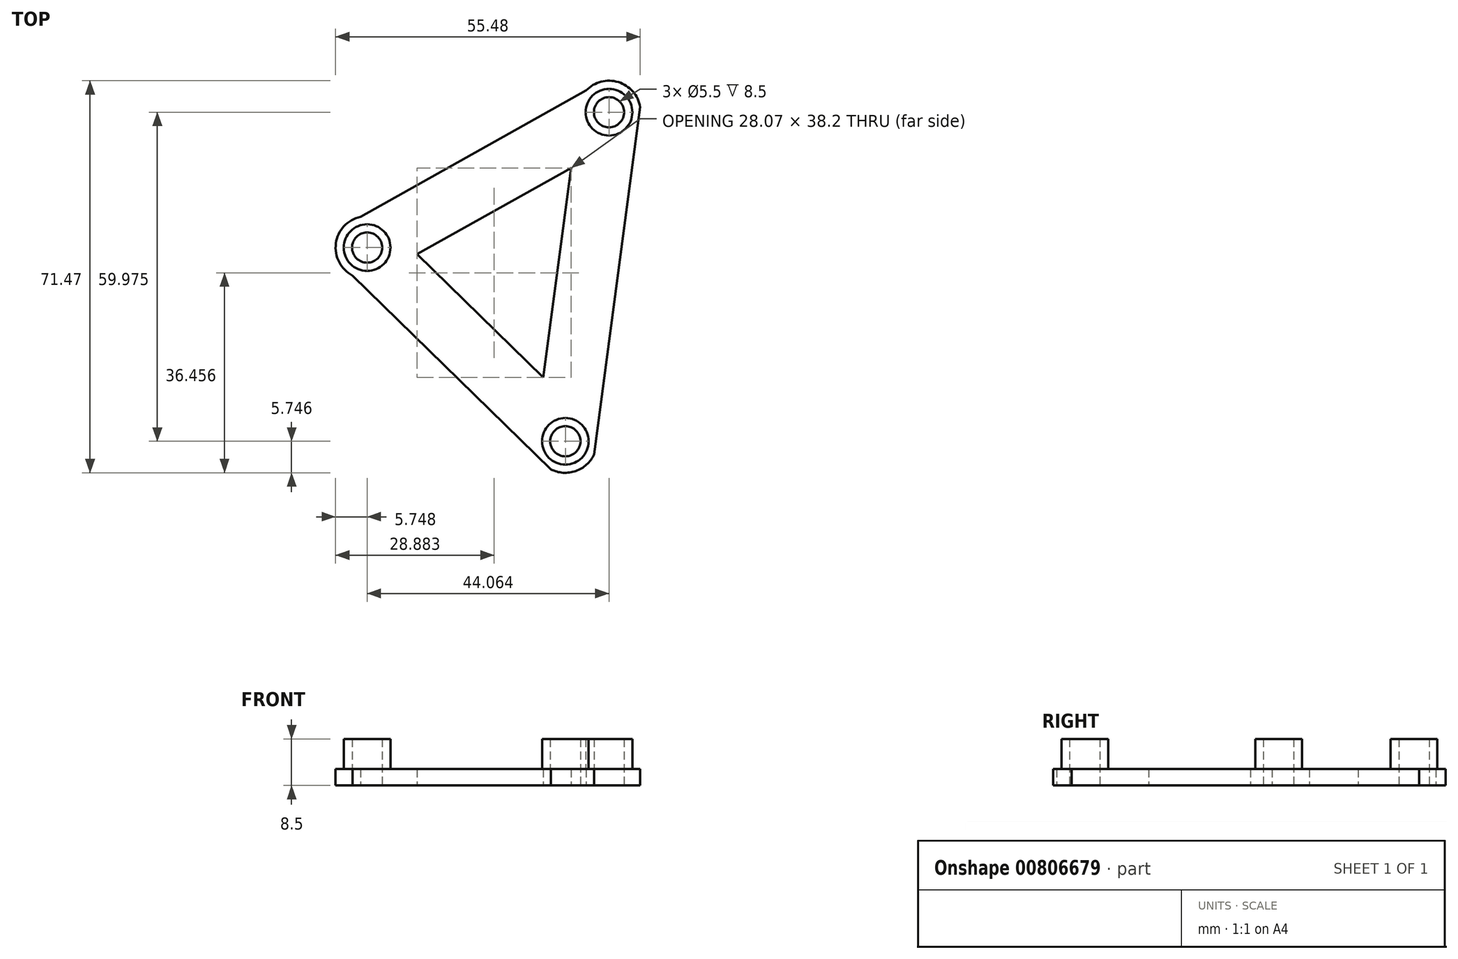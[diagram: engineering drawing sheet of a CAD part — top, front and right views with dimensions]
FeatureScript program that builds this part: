
annotation { "Feature Type Name" : "Feature", "Feature Type Description" : "" }
export const myFeature = defineFeature(function(context is Context, id is Id, definition is map)
    precondition{}
    {
        {
            var Q0;
            Q0=qCreatedBy(makeId("Top.planeOp"),FACE);
            var sketch = newSketch(context, id + "F0", { "sketchPlane" : qUnion([Q0])});
            skCircle(sketch, "E0", {"center": v(-17.4, 0) * mm, "radius": 2.75 * mm});
            skCircle(sketch, "E1", {"center": v(-17.4, 0) * mm, "radius": 5.75 * mm});
            skCircle(sketch, "E2", {"center": v(26.66, 24.67) * mm, "radius": 2.75 * mm});
            skCircle(sketch, "E3", {"center": v(26.66, 24.67) * mm, "radius": 5.75 * mm});
            skCircle(sketch, "E4", {"center": v(18.7, -35.3) * mm, "radius": 2.75 * mm});
            skCircle(sketch, "E5", {"center": v(18.7, -35.3) * mm, "radius": 5.75 * mm});
            skLineSegment(sketch, "E6", {"start": v(-17.4, 0) * mm, "end": v(26.66, 24.67) * mm, "construction": true});
            skLineSegment(sketch, "E7", {"start": v(-17.4, 0) * mm, "end": v(18.7, -35.3) * mm, "construction": true});
            skLineSegment(sketch, "E8", {"start": v(26.66, 24.67) * mm, "end": v(18.7, -35.3) * mm, "construction": true});
            skCircle(sketch, "E9", {"center": v(-17.4, 0) * mm, "radius": 4.25 * mm});
            skCircle(sketch, "E10", {"center": v(26.66, 24.67) * mm, "radius": 4.25 * mm});
            skCircle(sketch, "E11", {"center": v(18.7, -35.3) * mm, "radius": 4.25 * mm});
            skLineSegment(sketch, "E12.0", {"start": v(-8.3, -1.2) * mm, "end": v(19.77, 14.5) * mm});
            skLineSegment(sketch, "E12.1", {"start": v(-8.3, -1.2) * mm, "end": v(14.7, -23.7) * mm});
            skLineSegment(sketch, "E12.2", {"start": v(19.77, 14.5) * mm, "end": v(14.7, -23.7) * mm});
            skLineSegment(sketch, "E13.0", {"start": v(-18.63, 5.62) * mm, "end": v(22.51, 28.65) * mm});
            skLineSegment(sketch, "E13.1", {"start": v(-20.05, -5.1) * mm, "end": v(16.06, -40.4) * mm});
            skLineSegment(sketch, "E13.2", {"start": v(32.33, 25.61) * mm, "end": v(23.94, -37.69) * mm});
            skSolve(sketch);
        }
        {
            var Q0;
            Q0=makeQuery(id+"F0.imprint","IMPRINT",FACE,{"disambiguationData":[TD([[makeQuery(id+"F0.imprint","IMPRINT",EDGE,{"derivedFrom":sQuery(id+"F0.wireOp",EDGE,"E2")}),-1.0]])]});
            var Q1;
            {var subQ0=sQuery(id+"F0.wireOp",EDGE,"4292a800-b917-446e-8acb-4b11a4841fbd.0");var subQ1=sQuery(id+"F0.wireOp",EDGE,"E3");var subQ2=makeQuery(id+"F0.imprint","INTERSECT",VERTEX,{"derivedFrom":[subQ1,subQ0]});Q1=makeQuery(id+"F0.imprint","IMPRINT",FACE,{"disambiguationData":[TD([[makeQuery(id+"F0.imprint","IMPRINT",EDGE,{"disambiguationData":[TD([[subQ2,1.0]])],"derivedFrom":subQ1}),-1.0]])]});}
            var Q2;
            {var subQ0=sQuery(id+"F0.wireOp",EDGE,"b792d51c-0fe7-4bc2-b237-ce6525926208.0");Q2=makeQuery(id+"F0.imprint","IMPRINT",FACE,{"disambiguationData":[TD([[makeQuery(id+"F0.imprint","IMPRINT",EDGE,{"derivedFrom":subQ0}),-1.0]])]});}
            var Q3;
            Q3=makeQuery(id+"F0.imprint","IMPRINT",FACE,{"disambiguationData":[TD([[makeQuery(id+"F0.imprint","IMPRINT",EDGE,{"derivedFrom":sQuery(id+"F0.wireOp",EDGE,"E0")}),-1.0]])]});
            var Q4;
            {var subQ5=sQuery(id+"F0.wireOp",EDGE,"534e31a0-9855-4669-a3b1-e7b8400ff121.0");Q4=makeQuery(id+"F0.imprint","IMPRINT",FACE,{"disambiguationData":[TD([[makeQuery(id+"F0.imprint","IMPRINT",EDGE,{"derivedFrom":subQ5}),1.0]])]});}
            var Q5;
            {var subQ0=sQuery(id+"F0.wireOp",EDGE,"4292a800-b917-446e-8acb-4b11a4841fbd.0");var subQ1=sQuery(id+"F0.wireOp",EDGE,"E1");var subQ2=makeQuery(id+"F0.imprint","INTERSECT",VERTEX,{"derivedFrom":[subQ1,subQ0]});Q5=makeQuery(id+"F0.imprint","IMPRINT",FACE,{"disambiguationData":[TD([[makeQuery(id+"F0.imprint","IMPRINT",EDGE,{"disambiguationData":[TD([[subQ2,-1.0]])],"derivedFrom":subQ1}),-1.0]])]});}
            var Q6;
            {var subQ0=sQuery(id+"F0.wireOp",EDGE,"38d55559-1d0e-4463-9ff6-01328a6df294.0");var subQ1=sQuery(id+"F0.wireOp",EDGE,"E5");var subQ2=makeQuery(id+"F0.imprint","INTERSECT",VERTEX,{"derivedFrom":[subQ1,subQ0]});Q6=makeQuery(id+"F0.imprint","IMPRINT",FACE,{"disambiguationData":[TD([[makeQuery(id+"F0.imprint","IMPRINT",EDGE,{"disambiguationData":[TD([[subQ2,-1.0]])],"derivedFrom":subQ1}),-1.0]])]});}
            var Q7;
            Q7=makeQuery(id+"F0.imprint","IMPRINT",FACE,{"disambiguationData":[TD([[makeQuery(id+"F0.imprint","IMPRINT",EDGE,{"derivedFrom":sQuery(id+"F0.wireOp",EDGE,"E4")}),-1.0]])]});
            var Q8;
            {var subQ9=sQuery(id+"F0.wireOp",EDGE,"a9f5d0ef-61d3-43a7-a030-e22b1175c3c5.0");Q8=makeQuery(id+"F0.imprint","IMPRINT",FACE,{"disambiguationData":[TD([[makeQuery(id+"F0.imprint","IMPRINT",EDGE,{"derivedFrom":subQ9}),-1.0]])]});}
            var Q9;
            Q9=makeQuery(id+"F0.imprint","IMPRINT",FACE,{"disambiguationData":[TD([[makeQuery(id+"F0.imprint","IMPRINT",EDGE,{"derivedFrom":sQuery(id+"F0.wireOp",EDGE,"E11")}),-1.0]])]});
            var Q10;
            Q10=makeQuery(id+"F0.imprint","IMPRINT",FACE,{"disambiguationData":[TD([[makeQuery(id+"F0.imprint","IMPRINT",EDGE,{"derivedFrom":sQuery(id+"F0.wireOp",EDGE,"E9")}),-1.0]])]});
            var Q11;
            Q11=makeQuery(id+"F0.imprint","IMPRINT",FACE,{"disambiguationData":[TD([[makeQuery(id+"F0.imprint","IMPRINT",EDGE,{"derivedFrom":sQuery(id+"F0.wireOp",EDGE,"E10")}),-1.0]])]});
            extrude(context, id + "F1", {"entities" : qUnion([Q0, Q1, Q2, Q3, Q4, Q5, Q6, Q7, Q8, Q9, Q10, Q11]), "depth" : 3 * mm, "offsetDistance" : 25 * mm});
        }
        {
            var Q0;
            Q0=makeQuery(id+"F0.imprint","IMPRINT",FACE,{"disambiguationData":[TD([[makeQuery(id+"F0.imprint","IMPRINT",EDGE,{"derivedFrom":sQuery(id+"F0.wireOp",EDGE,"E2")}),-1.0]])]});
            var Q1;
            Q1=makeQuery(id+"F0.imprint","IMPRINT",FACE,{"disambiguationData":[TD([[makeQuery(id+"F0.imprint","IMPRINT",EDGE,{"derivedFrom":sQuery(id+"F0.wireOp",EDGE,"E0")}),-1.0]])]});
            var Q2;
            Q2=makeQuery(id+"F0.imprint","IMPRINT",FACE,{"disambiguationData":[TD([[makeQuery(id+"F0.imprint","IMPRINT",EDGE,{"derivedFrom":sQuery(id+"F0.wireOp",EDGE,"E4")}),-1.0]])]});
            extrude(context, id + "F2", {"entities" : qUnion([Q0, Q1, Q2]), "operationType" : NewBodyOperationType.ADD, "depth" : 8.5 * mm, "offsetDistance" : 25 * mm});
        }
    });
